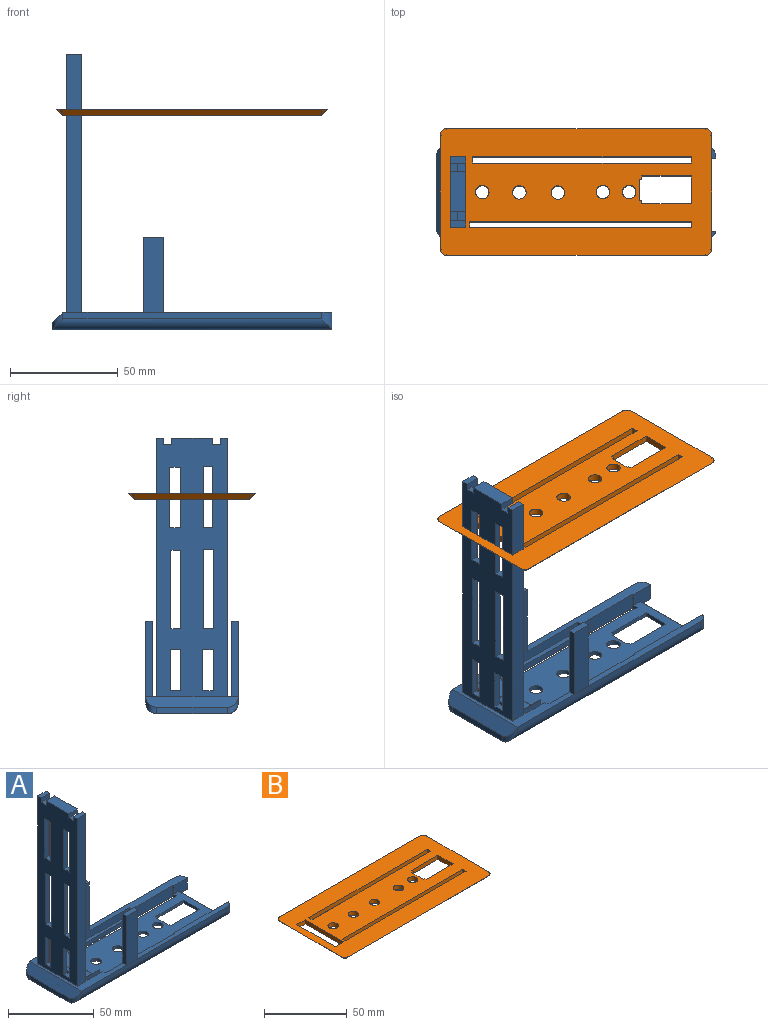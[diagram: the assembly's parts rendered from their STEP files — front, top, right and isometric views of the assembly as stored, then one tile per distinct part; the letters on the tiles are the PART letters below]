
ASSEMBLY  parts=2 mates=1
PART A: 121 faces, bbox 132.1x45.1x130.1 mm
  f0: plane 125x43mm, normal (0,0,1), area 658.8mm2, adj f2,f3,f17,f20,f22,f23,f24,f26
  f1: plane 78.48x5.72mm, normal (0,0,1), area 332.6mm2, adj f4,f7,f19,f24,f27,f91,f92,f109
  f2: plane 27.27x6.07mm, normal (1,0,0), area 41.3mm2, adj f0,f8,f33,f35,f36,f82,f84,f90
  f3: plane 5x2.11mm, normal (1,0,0), area 10.5mm2, adj f0,f5,f27,f92
  f4: plane 5x2.11mm, normal (-1,0,0), area 10.5mm2, adj f1,f5,f27,f92
  f5: plane 56x2.11mm, normal (0,0,1), area 118.1mm2, adj f3,f4,f27,f92
  f6: plane 130x33mm, normal (0,0,-1), area 3099.5mm2, adj f7,f19,f25,f76,f85,f86,f87,f89
  f7: plane 11.4x8mm, normal (0,-1,0), area 80.8mm2, adj f1,f6,f8,f19,f76,f91
  f8: plane 95x33.8mm, normal (0,0,1), area 2335.1mm2, adj f2,f7,f23,f32,f76,f86,f89,f90
  f9: plane 4.86x0.1mm, normal (1,0,0), area 0.5mm2, adj f35,f36,f83,f85
  f10: plane 2.11x2mm, normal (-1,0,0), area 4.2mm2, adj f12,f13,f46,f92
  f11: plane 3.29x2mm, normal (-1,0,0), area 6.6mm2, adj f12,f13,f43,f90
  f12: plane 37x22mm, normal (0,0,-1), area 487.2mm2, adj f10,f11,f21,f40,f41,f42,f43,f44
  f13: plane 37x22mm, normal (0,0,1), area 594.3mm2, adj f10,f11,f41,f42,f43,f44,f45,f46
  f14: plane 7x3mm, normal (0,0,1), area 21mm2, adj f20,f22,f37,f49
  f15: plane 18.66x7mm, normal (0,0,1), area 130.6mm2, adj f16,f20,f78,f81
  f16: plane 18.66x3mm, normal (1,0,0), area 56mm2, adj f15,f18,f78,f81
  f17: plane 120x3mm, normal (1,0,0), area 360mm2, adj f0,f38,f39,f50,f79
  f18: plane 18.66x4mm, normal (0,0,-1), area 74.6mm2, adj f16,f21,f78,f81
  f19: plane 8x0.72mm, normal (1,0,0), area 5.8mm2, adj f1,f6,f7,f115
  f20: plane 120x32.78mm, normal (-1,0,0), area 3119mm2, adj f0,f14,f15,f37,f38,f39,f49,f51
  f21: plane 120.01x26.78mm, normal (1,0,0), area 2423.4mm2, adj f12,f18,f49,f50,f51,f52,f53,f54
  f22: plane 120x3mm, normal (1,0,0), area 360mm2, adj f0,f14,f37,f49
  f23: plane 6.07x1.63mm, normal (1,0,0), area 9.9mm2, adj f0,f8,f32,f89
  f24: plane 120x38mm, normal (0,1,0), area 678.9mm2, adj f0,f1,f108,f109,f110,f115,f116,f117
  f25: plane 33x3mm, normal (-1,0,0), area 99mm2, adj f6,f75,f117,f120
  f26: plane 120.24x3mm, normal (0,-1,0), area 360.7mm2, adj f0,f118,f119,f120
  f27: plane 56x40mm, normal (0,-1,0), area 598.9mm2, adj f0,f1,f3,f4,f5,f108,f109,f110
  f28: plane 5x0.48mm, normal (1,0,0), area 2.4mm2, adj f0,f29,f31,f32
  f29: plane 56x40mm, normal (0,1,0), area 604mm2, adj f0,f28,f30,f31,f111,f113,f114
  f30: plane 5x0.48mm, normal (-1,0,0), area 2.4mm2, adj f0,f29,f31,f32
  f31: plane 56x0.48mm, normal (0,0,1), area 26.6mm2, adj f28,f29,f30,f32
  f32: plane 102x7.76mm, normal (0,1,0), area 349.5mm2, adj f0,f8,f23,f28,f30,f31,f76,f118
  f33: plane 8.21x0.1mm, normal (0,-1,0), area 0.8mm2, adj f2,f34,f36,f82
  f34: plane 4.76x0.1mm, normal (1,0,0), area 0.5mm2, adj f33,f36,f83,f85
  f35: plane 8.21x0.1mm, normal (0,1,0), area 0.8mm2, adj f2,f9,f36,f84
  f36: plane 14.9x8.21mm, normal (0,0,1), area 97.2mm2, adj f2,f9,f33,f34,f35,f85
  f37: plane 120x7mm, normal (0,1,0), area 840mm2, adj f0,f14,f20,f22
  f38: plane 120x7mm, normal (0,-1,0), area 840mm2, adj f0,f17,f20,f39
  f39: plane 7x2.99mm, normal (0,0,1), area 20.9mm2, adj f17,f20,f38,f79
  f40: plane 26.78x3mm, normal (-1,0,0), area 80.3mm2, adj f0,f12,f49,f50
  f41: plane 20.9x2mm, normal (-1,0,0), area 41.8mm2, adj f12,f13,f42,f43
  f42: plane 8.21x2mm, normal (0,1,0), area 16.4mm2, adj f12,f13,f41,f44
  f43: plane 8.21x2mm, normal (0,-1,0), area 16.4mm2, adj f11,f12,f13,f41
  f44: plane 3.09x2mm, normal (-1,0,0), area 6.2mm2, adj f12,f13,f42,f95
  f45: plane 2.11x2mm, normal (-1,0,0), area 4.2mm2, adj f12,f13,f48,f89
  f46: plane 22x2mm, normal (0,-1,0), area 44mm2, adj f10,f12,f13,f47
  f47: plane 37x2mm, normal (1,0,0), area 74mm2, adj f12,f13,f46,f48
  f48: plane 22x2mm, normal (0,1,0), area 44mm2, adj f12,f13,f45,f47
  f49: plane 123x7mm, normal (0,-1,0), area 501mm2, adj f12,f14,f20,f21,f22,f40,f80
  f50: plane 120.03x4.02mm, normal (0,1,0), area 480mm2, adj f12,f17,f21,f40,f79
  f51: plane 4.67x3mm, normal (0,0,-1), area 14mm2, adj f20,f21,f52,f54
  f52: plane 19.36x3mm, normal (0,1,0), area 58.1mm2, adj f20,f21,f51,f53
  f53: plane 4.67x3mm, normal (0,0,1), area 14mm2, adj f20,f21,f52,f54
  f54: plane 19.36x3mm, normal (0,-1,0), area 58.1mm2, adj f20,f21,f51,f53
  f55: plane 4.51x3mm, normal (0,0,-1), area 13.5mm2, adj f20,f21,f56,f58
  f56: plane 28.41x3mm, normal (0,1,0), area 85.2mm2, adj f20,f21,f55,f57
  f57: plane 4.51x3mm, normal (0,0,1), area 13.5mm2, adj f20,f21,f56,f58
  f58: plane 28.41x3mm, normal (0,-1,0), area 85.2mm2, adj f20,f21,f55,f57
  f59: plane 5.07x3mm, normal (0,0,-1), area 15.2mm2, adj f20,f21,f60,f62
  f60: plane 19.1x3mm, normal (0,1,0), area 57.3mm2, adj f20,f21,f59,f61
  f61: plane 5.07x3mm, normal (0,0,1), area 15.2mm2, adj f20,f21,f60,f62
  f62: plane 19.1x3mm, normal (0,-1,0), area 57.3mm2, adj f20,f21,f59,f61
  f63: plane 4.5x3mm, normal (0,0,-1), area 13.5mm2, adj f20,f21,f64,f66
  f64: plane 36.44x3mm, normal (0,1,0), area 109.3mm2, adj f20,f21,f63,f65
  f65: plane 4.5x3mm, normal (0,0,1), area 13.5mm2, adj f20,f21,f64,f66
  f66: plane 36.44x3mm, normal (0,-1,0), area 109.3mm2, adj f20,f21,f63,f65
  f67: plane 4.72x3mm, normal (0,0,-1), area 14.1mm2, adj f20,f21,f68,f70
  f68: plane 36.76x3mm, normal (0,1,0), area 110.3mm2, adj f20,f21,f67,f69
  f69: plane 4.72x3mm, normal (0,0,1), area 14.1mm2, adj f20,f21,f68,f70
  f70: plane 36.76x3mm, normal (0,-1,0), area 110.3mm2, adj f20,f21,f67,f69
  f71: plane 4.91x3mm, normal (0,0,-1), area 14.7mm2, adj f20,f21,f72,f74
  f72: plane 28.03x3mm, normal (0,1,0), area 84.1mm2, adj f20,f21,f71,f73
  f73: plane 4.91x3mm, normal (0,0,1), area 14.7mm2, adj f20,f21,f72,f74
  f74: plane 28.03x3mm, normal (0,-1,0), area 84.1mm2, adj f20,f21,f71,f73
  f75: plane 45.1x7.1mm, normal (-0.71,0,0.71), area 288.9mm2, adj f0,f25,f117,f120
  f76: plane 33.92x2.05mm, normal (0.71,0,0.71), area 92.1mm2, adj f6,f7,f8,f32,f119
  f77: plane 4.06x3mm, normal (0,0,1), area 12.2mm2, adj f20,f21,f78,f79
  f78: plane 7x3mm, normal (0,-1,0), area 20.9mm2, adj f15,f16,f18,f20,f77
  f79: plane 7.02x3.01mm, normal (0,1,0), area 20.9mm2, adj f17,f20,f39,f50,f77
  f80: plane 4.06x3mm, normal (0,0,1), area 12.2mm2, adj f20,f21,f49,f81
  f81: plane 7x3mm, normal (0,1,0), area 21mm2, adj f15,f16,f18,f20,f80
  f82: plane 14.11x5.9mm, normal (0,-0.71,0.71), area 93.1mm2, adj f0,f2,f33,f83
  f83: plane 26.7x5.9mm, normal (0.71,0,0.71), area 165.9mm2, adj f0,f9,f34,f82,f84,f85
  f84: plane 14.11x5.9mm, normal (0,0.71,0.71), area 93.1mm2, adj f0,f2,f35,f83
  f85: cylinder r=3.12mm len=6.24mm, axis (0,0,1), area 45.8mm2, adj f6,f9,f34,f36,f83
  f86: plane 2.6x1.93mm, normal (-1,0,0), area 5mm2, adj f6,f8,f89,f90
  f87: plane 3x2.6mm, normal (1,0,0), area 7.8mm2, adj f6,f13,f89,f90
  f88: plane 3x2.6mm, normal (1,0,0), area 7.8mm2, adj f0,f12,f89,f90
  f89: plane 103.24x8mm, normal (0,1,0), area 255.9mm2, adj f0,f6,f8,f12,f13,f23,f45,f86
  f90: plane 103.24x8mm, normal (0,-1,0), area 255.9mm2, adj f0,f2,f6,f8,f11,f12,f13,f86
  f91: plane 8x2.91mm, normal (-1,0,0), area 9.3mm2, adj f1,f6,f7,f8,f92,f95
  f92: plane 101.69x8mm, normal (0,-1,0), area 517.3mm2, adj f0,f1,f3,f4,f5,f6,f10,f12
  f93: plane 3x2.91mm, normal (1,0,0), area 8.7mm2, adj f6,f13,f92,f95
  f94: plane 3x2.91mm, normal (1,0,0), area 8.7mm2, adj f0,f12,f92,f95
  f95: plane 101.69x8mm, normal (0,1,0), area 247.4mm2, adj f0,f2,f6,f8,f12,f13,f44,f91
  f96: plane 1.93x1.06mm, normal (0,1,0), area 2.1mm2, adj f6,f8,f97,f103
  f97: plane 1.93x1.46mm, normal (1,0,0), area 2.8mm2, adj f6,f8,f96,f98
  f98: plane 23x1.93mm, normal (0,1,0), area 44.4mm2, adj f6,f8,f97,f99
  f99: plane 13x1.93mm, normal (-1,0,0), area 25.1mm2, adj f6,f8,f98,f100
  f100: plane 23x1.93mm, normal (0,-1,0), area 44.4mm2, adj f6,f8,f99,f101
  f101: plane 1.93x1.68mm, normal (1,0,0), area 3.3mm2, adj f6,f8,f100,f102
  f102: plane 1.93x1.06mm, normal (0,-1,0), area 2.1mm2, adj f6,f8,f101,f103
  f103: plane 9.85x1.93mm, normal (1,0,0), area 19mm2, adj f6,f8,f96,f102
  f104: cylinder r=3.12mm len=6.24mm, axis (0,0,1), area 37.8mm2, adj f6,f8
  f105: cylinder r=3.12mm len=6.24mm, axis (0,0,1), area 37.8mm2, adj f6,f8
  f106: cylinder r=3.12mm len=6.24mm, axis (0,0,1), area 37.8mm2, adj f6,f8
  f107: cylinder r=3.12mm len=6.24mm, axis (0,0,1), area 37.8mm2, adj f6,f8
  f108: plane 35x3mm, normal (-1,0,0), area 105mm2, adj f0,f24,f27,f110
  f109: plane 35x3mm, normal (1,0,0), area 105mm2, adj f1,f24,f27,f110
  f110: plane 9.11x3mm, normal (0,0,1), area 27.3mm2, adj f24,f27,f108,f109
  f111: plane 35x2.98mm, normal (-1,0,0), area 104.3mm2, adj f0,f29,f112,f114
  f112: plane 35x9.26mm, normal (0,-1,0), area 324mm2, adj f0,f111,f113,f114
  f113: plane 35x2.98mm, normal (1,0,0), area 104.3mm2, adj f0,f29,f112,f114
  f114: plane 9.26x2.98mm, normal (0,0,1), area 27.6mm2, adj f29,f111,f112,f113
  f115: cylinder r=5mm len=8mm, axis (0,0,1), area 43.2mm2, adj f1,f19,f24,f116
  f116: cylinder r=5mm len=130mm, axis (1,0,0), area 981.7mm2, adj f6,f24,f115,f117
  f117: cylinder r=5mm len=8mm, axis (0,0,-1), area 23.6mm2, adj f24,f25,f75,f116
  f118: cylinder r=5mm len=7.76mm, axis (0,0,1), area 33.9mm2, adj f0,f26,f32,f119
  f119: cylinder r=5mm len=130mm, axis (-1,0,0), area 983.7mm2, adj f6,f26,f32,f76,f118,f120
  f120: cylinder r=5mm len=8mm, axis (0,0,1), area 23.6mm2, adj f25,f26,f75,f119
PART B: 35 faces, bbox 126x59x3 mm
  f0: plane 126x59mm, normal (0,0,1), area 6169.9mm2, adj f2,f3,f4,f5,f6,f7,f8,f9
  f1: plane 120x53mm, normal (0,0,-1), area 5103.6mm2, adj f2,f3,f4,f5,f6,f7,f8,f9
  f2: plane 7x3mm, normal (0,-1,0), area 21mm2, adj f0,f1,f3,f5
  f3: plane 32.78x3mm, normal (-1,0,0), area 98.3mm2, adj f0,f1,f2,f4
  f4: plane 7x3mm, normal (0,1,0), area 21mm2, adj f0,f1,f3,f5
  f5: plane 32.78x3mm, normal (1,0,0), area 98.3mm2, adj f0,f1,f2,f4
  f6: plane 3x1.06mm, normal (0,1,0), area 3.2mm2, adj f0,f1,f7,f13
  f7: plane 3x1.46mm, normal (1,0,0), area 4.4mm2, adj f0,f1,f6,f8
  f8: plane 23x3mm, normal (0,1,0), area 69mm2, adj f0,f1,f7,f9
  f9: plane 13x3mm, normal (-1,0,0), area 39mm2, adj f0,f1,f8,f10
  f10: plane 23x3mm, normal (0,-1,0), area 69mm2, adj f0,f1,f9,f11
  f11: plane 3x1.68mm, normal (1,0,0), area 5.1mm2, adj f0,f1,f10,f12
  f12: plane 3x1.06mm, normal (0,-1,0), area 3.2mm2, adj f0,f1,f11,f13
  f13: plane 9.85x3mm, normal (1,0,0), area 29.6mm2, adj f0,f1,f6,f12
  f14: plane 3x2.6mm, normal (1,0,0), area 7.8mm2, adj f0,f1,f15,f17
  f15: plane 103.24x3mm, normal (0,1,0), area 309.7mm2, adj f0,f1,f14,f16
  f16: plane 3x2.6mm, normal (-1,0,0), area 7.8mm2, adj f0,f1,f15,f17
  f17: plane 103.24x3mm, normal (0,-1,0), area 309.7mm2, adj f0,f1,f14,f16
  f18: plane 101.69x3mm, normal (0,-1,0), area 305.1mm2, adj f0,f1,f19,f21
  f19: plane 3x2.91mm, normal (1,0,0), area 8.7mm2, adj f0,f1,f18,f20
  f20: plane 101.69x3mm, normal (0,1,0), area 305.1mm2, adj f0,f1,f19,f21
  f21: plane 3x2.91mm, normal (-1,0,0), area 8.7mm2, adj f0,f1,f18,f20
  f22: cylinder r=3.12mm len=6.24mm, axis (0,0,1), area 58.8mm2, adj f0,f1
  f23: cylinder r=3.12mm len=6.24mm, axis (0,0,1), area 58.8mm2, adj f0,f1
  f24: cylinder r=3.12mm len=6.24mm, axis (0,0,1), area 58.8mm2, adj f0,f1
  f25: cylinder r=3.12mm len=6.24mm, axis (0,0,1), area 58.8mm2, adj f0,f1
  f26: cylinder r=3.12mm len=6.24mm, axis (0,0,1), area 58.8mm2, adj f0,f1
  f27: plane 53x3mm, normal (0.71,0,-0.71), area 224.9mm2, adj f0,f1,f28,f29
  f28: cone r=5mm half-angle=45deg, axis (0,0,1), area 10mm2, adj f0,f27,f30
  f29: cone r=5mm half-angle=45deg, axis (0,0,1), area 10mm2, adj f0,f27,f31
  f30: plane 120x3mm, normal (0,0.71,-0.71), area 509.1mm2, adj f0,f1,f28,f32
  f31: plane 120x3mm, normal (0,-0.71,-0.71), area 509.1mm2, adj f0,f1,f29,f33
  f32: cone r=5mm half-angle=45deg, axis (0,0,1), area 10mm2, adj f0,f30,f34
  f33: cone r=5mm half-angle=45deg, axis (0,0,1), area 10mm2, adj f0,f31,f34
  f34: plane 53x3mm, normal (-0.71,0,-0.71), area 224.9mm2, adj f0,f1,f32,f33
PLACE A at identity fixed
PLACE B t=(0,0,-48.48)mm
MATE slider A.f15 <-> B.f1  axis (0,0,1) through (-50.95,7.55,120)mm
